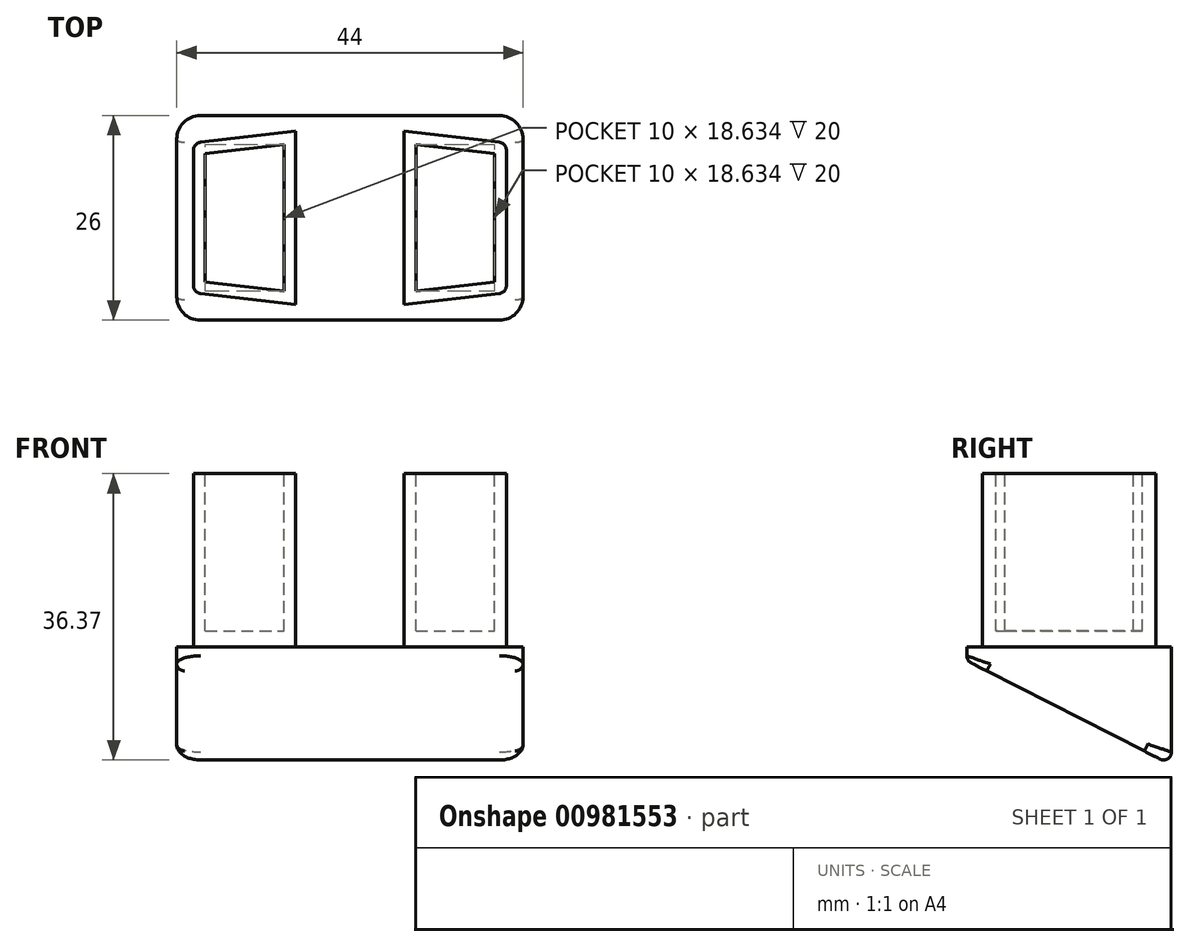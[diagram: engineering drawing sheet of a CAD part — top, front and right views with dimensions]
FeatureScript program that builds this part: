
annotation { "Feature Type Name" : "Feature", "Feature Type Description" : "" }
export const myFeature = defineFeature(function(context is Context, id is Id, definition is map)
    precondition{}
    {
        {
            var Q0;
            Q0=qCreatedBy(makeId("Top.planeOp"),FACE);
            var sketch = newSketch(context, id + "F0", { "sketchPlane" : qUnion([Q0])});
            skLineSegment(sketch, "E0.bottom", {"start": v(22, -13) * mm, "end": v(-22, -13) * mm});
            skLineSegment(sketch, "E0.top", {"start": v(22, 13) * mm, "end": v(-22, 13) * mm});
            skLineSegment(sketch, "E0.left", {"start": v(22, -13) * mm, "end": v(22, 13) * mm});
            skLineSegment(sketch, "E0.right", {"start": v(-22, -13) * mm, "end": v(-22, 13) * mm});
            skPoint(sketch, "E0.middle", {"position": v(0, 0) * mm});
            skSolve(sketch);
        }
        {
            var Q0;
            Q0=qSketchRegion(id+"F0",true);
            extrude(context, id + "F1", {"entities" : qUnion([Q0]), "depth" : 15 * mm, "offsetDistance" : 25 * mm});
        }
        {
            var Q0;
            Q0=makeQuery(id+"F1.opExtrude","CAP_FACE",FACE,{"disambiguationData":[OSD([sQuery(id+"F0.wireOp",EDGE,"E0.bottom"),sQuery(id+"F0.wireOp",EDGE,"E0.top"),sQuery(id+"F0.wireOp",EDGE,"E0.left"),sQuery(id+"F0.wireOp",EDGE,"E0.right")])],"isStart":false});
            var sketch = newSketch(context, id + "F2", { "sketchPlane" : qUnion([Q0])});
            skPoint(sketch, "E1.0", {"position": v(0, 0) * mm});
            skLineSegment(sketch, "E2", {"start": v(6.88, -11) * mm, "end": v(6.88, 11) * mm});
            skLineSegment(sketch, "E3", {"start": v(6.88, 11) * mm, "end": v(18.99, 9.6) * mm});
            skLineSegment(sketch, "E4", {"start": v(19.88, 8.6) * mm, "end": v(19.88, -8.6) * mm});
            skLineSegment(sketch, "E5", {"start": v(18.99, -9.6) * mm, "end": v(6.87, -11) * mm});
            skLineSegment(sketch, "E6", {"start": v(0, 0) * mm, "end": v(22, 0) * mm, "construction": true});
            skPoint(sketch, "E7.visualSharp", {"position": v(19.88, 9.5) * mm});
            skArc(sketch, "E7.filletArc", {"start": v(19.88, 8.6) * mm, "mid": v(19.62, 9.27) * mm, "end": v(18.99, 9.6) * mm});
            skPoint(sketch, "E8.visualSharp", {"position": v(19.88, -9.5) * mm});
            skArc(sketch, "E8.filletArc", {"start": v(18.99, -9.6) * mm, "mid": v(19.62, -9.27) * mm, "end": v(19.88, -8.6) * mm});
            skLineSegment(sketch, "E9.MirrorCS", {"start": v(-6.88, -11) * mm, "end": v(-6.88, 11) * mm});
            skLineSegment(sketch, "E10.MirrorCS", {"start": v(-6.88, 11) * mm, "end": v(-18.99, 9.6) * mm});
            skLineSegment(sketch, "E11.MirrorCS", {"start": v(-19.88, 8.6) * mm, "end": v(-19.88, -8.6) * mm});
            skLineSegment(sketch, "E12.MirrorCS", {"start": v(-18.99, -9.6) * mm, "end": v(-6.87, -11) * mm});
            skArc(sketch, "E13.MirrorCS", {"start": v(-19.88, 8.6) * mm, "mid": v(-19.62, 9.27) * mm, "end": v(-18.99, 9.6) * mm});
            skPoint(sketch, "E14.MirrorP", {"position": v(-19.88, 9.5) * mm});
            skArc(sketch, "E15.MirrorCS", {"start": v(-18.99, -9.6) * mm, "mid": v(-19.62, -9.27) * mm, "end": v(-19.88, -8.6) * mm});
            skPoint(sketch, "E16.MirrorP", {"position": v(-19.88, -9.5) * mm});
            skSolve(sketch);
        }
        {
            var Q0;
            Q0=qSketchRegion(id+"F2",true);
            var Q1;
            Q1=makeQuery(id+"F2.imprint","IMPRINT",FACE,{"disambiguationData":[TD([[makeQuery(id+"F2.imprint","IMPRINT",EDGE,{"derivedFrom":sQuery(id+"F2.wireOp",EDGE,"E2")}),-1.0]])]});
            extrude(context, id + "F3", {"entities" : qUnion([Q0, Q1]), "operationType" : NewBodyOperationType.ADD, "depth" : 22 * mm, "offsetDistance" : 25 * mm});
        }
        {
            var Q0;
            Q0=makeQuery(id+"F1.opExtrude","SWEPT_EDGE",EDGE,{"disambiguationData":[OSD([sQuery(id+"F0.wireOp",EDGE,"E0.top"),sQuery(id+"F0.wireOp",EDGE,"E0.left")])]});
            var Q1;
            Q1=makeQuery(id+"F1.opExtrude","SWEPT_EDGE",EDGE,{"disambiguationData":[OSD([sQuery(id+"F0.wireOp",EDGE,"E0.top"),sQuery(id+"F0.wireOp",EDGE,"E0.right")])]});
            var Q2;
            Q2=makeQuery(id+"F1.opExtrude","SWEPT_EDGE",EDGE,{"disambiguationData":[OSD([sQuery(id+"F0.wireOp",EDGE,"E0.bottom"),sQuery(id+"F0.wireOp",EDGE,"E0.left")])]});
            var Q3;
            Q3=makeQuery(id+"F1.opExtrude","SWEPT_EDGE",EDGE,{"disambiguationData":[OSD([sQuery(id+"F0.wireOp",EDGE,"E0.bottom"),sQuery(id+"F0.wireOp",EDGE,"E0.right")])]});
            fillet(context, id + "F4", {"entities" : qUnion([Q0, Q1, Q2, Q3]), "radius" : 3 * mm, "tangentPropagation" : true, "allowEdgeOverflow" : false});
        }
        {
            var Q0;
            Q0=makeQuery(id+"F3.opExtrude","CAP_FACE",FACE,{"disambiguationData":[OSD([sQuery(id+"F2.wireOp",EDGE,"E2"),sQuery(id+"F2.wireOp",EDGE,"E3"),sQuery(id+"F2.wireOp",EDGE,"E4"),sQuery(id+"F2.wireOp",EDGE,"E5"),sQuery(id+"F2.wireOp",EDGE,"E7.filletArc"),sQuery(id+"F2.wireOp",EDGE,"E8.filletArc")])],"isStart":false});
            var sketch = newSketch(context, id + "F5", { "sketchPlane" : qUnion([Q0])});
            skLineSegment(sketch, "E17.0.2", {"start": v(19.6, 9.53) * mm, "end": v(6.87, 11) * mm, "construction": true});
            skLineSegment(sketch, "E17.0.3", {"start": v(6.88, 11) * mm, "end": v(6.88, -11) * mm, "construction": true});
            skLineSegment(sketch, "E18.0", {"start": v(18.38, -8.16) * mm, "end": v(18.38, 8.16) * mm});
            skLineSegment(sketch, "E18.1", {"start": v(8.38, -9.32) * mm, "end": v(18.38, -8.16) * mm});
            skLineSegment(sketch, "E18.2", {"start": v(8.38, 9.32) * mm, "end": v(8.38, -9.32) * mm});
            skLineSegment(sketch, "E18.3", {"start": v(18.38, 8.16) * mm, "end": v(8.38, 9.32) * mm});
            skPoint(sketch, "E19.0", {"position": v(0, 0) * mm});
            skLineSegment(sketch, "E20.MirrorCS", {"start": v(-18.38, 8.16) * mm, "end": v(-8.38, 9.32) * mm});
            skLineSegment(sketch, "E21.MirrorCS", {"start": v(-8.38, 9.32) * mm, "end": v(-8.38, -9.32) * mm});
            skLineSegment(sketch, "E22.MirrorCS", {"start": v(-8.38, -9.32) * mm, "end": v(-18.38, -8.16) * mm});
            skLineSegment(sketch, "E23.MirrorCS", {"start": v(-18.38, -8.16) * mm, "end": v(-18.38, 8.16) * mm});
            skSolve(sketch);
        }
        {
            var Q0;
            Q0=makeQuery(id+"F5.imprint","IMPRINT",FACE,{"disambiguationData":[TD([[makeQuery(id+"F5.imprint","IMPRINT",EDGE,{"derivedFrom":sQuery(id+"F5.wireOp",EDGE,"E20.MirrorCS")}),-1.0]])]});
            var Q1;
            Q1=makeQuery(id+"F5.imprint","IMPRINT",FACE,{"disambiguationData":[TD([[makeQuery(id+"F5.imprint","IMPRINT",EDGE,{"derivedFrom":sQuery(id+"F5.wireOp",EDGE,"E18.0")}),1.0]])]});
            extrude(context, id + "F6", {"entities" : qUnion([Q0, Q1]), "operationType" : NewBodyOperationType.REMOVE, "oppositeDirection" : true, "depth" : 20 * mm, "offsetDistance" : 25 * mm});
        }
        {
            var Q0;
            Q0=makeQuery(id+"F1.opExtrude","SWEPT_FACE",FACE,{"disambiguationData":[OSD([sQuery(id+"F0.wireOp",EDGE,"E0.left")])]});
            var sketch = newSketch(context, id + "F7", { "sketchPlane" : qUnion([Q0]), "disableImprinting" : false});
            skLineSegment(sketch, "E24", {"start": v(13, 0) * mm, "end": v(-13, 13.25) * mm});
            skLineSegment(sketch, "E25", {"start": v(-13, 13.25) * mm, "end": v(-13, 0) * mm});
            skLineSegment(sketch, "E26", {"start": v(-13, 0) * mm, "end": v(13, 0) * mm});
            skSolve(sketch);
        }
        {
            var Q0;
            Q0=qSketchRegion(id+"F7",true);
            extrude(context, id + "F8", {"entities" : qUnion([Q0]), "operationType" : NewBodyOperationType.REMOVE, "oppositeDirection" : true, "depth" : 44 * mm, "offsetDistance" : 25 * mm});
        }
        {
            var Q0;
            Q0=makeQuery(id+"F8.boolean.opBoolean","MERGE",EDGE,{"derivedFrom":[makeQuery(id+"F1.opExtrude","CAP_EDGE",EDGE,{"disambiguationData":[OSD([sQuery(id+"F0.wireOp",EDGE,"E0.top")])],"isStart":true})],"fromTools":[makeQuery(id+"F8.opExtrude","SWEPT_EDGE",EDGE,{"disambiguationData":[OSD([sQuery(id+"F7.wireOp",EDGE,"E24"),sQuery(id+"F7.wireOp",EDGE,"E26")])]})]});
            fillet(context, id + "F9", {"entities" : qUnion([Q0]), "radius" : 1 * mm, "tangentPropagation" : true, "allowEdgeOverflow" : false});
        }
    });
